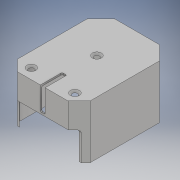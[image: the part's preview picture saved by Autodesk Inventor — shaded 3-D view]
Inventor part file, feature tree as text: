
AUTODESK INVENTOR PART (.ipt)
format: ipt  version: 2017 (Build 210142000, 142)  size: 454,144 bytes
history: native  units: mm
features: extrude x9, sketch x7, other x5, fillet x4, hole x3
ambient origin geometry x8: Origin, YZ Plane, XZ Plane, XY Plane, X Axis, Y Axis, Z Axis, Center Point
bodies: Body1 (feature_tree)
feature tree (28):
  other  "Твердое тело1"
  sketch  "Эскиз1"
  extrude  "Выдавливание1"  Depth=58.6mm
  extrude  "Выдавливание2"  Depth=77.0mm
  fillet  "Сопряжение1"  Radius=11.0mm
  extrude  "Выдавливание3"  Depth=11.0mm
  extrude  "Выдавливание4"  Depth=8.5mm
  extrude  "Выдавливание5"  Depth=8.5mm
  other  "Комбинировать1"
  hole  "Отверстие4"  [1 undecoded]
  hole  "Отверстие5"  [1 undecoded]
  hole  "Отверстие6"  [1 undecoded]
  fillet  "Сопряжение2"  Radius=11.0mm
  fillet  "Сопряжение3"  Radius=1.2mm
  extrude  "Выдавливание6"  Depth=1.5mm TaperAngle=0.0deg
  extrude  "Выдавливание7"  Depth=43.5mm TaperAngle=0.0deg
  extrude  "Выдавливание8"  Depth=1.0mm
  other  "Комбинировать2"
  fillet  "Сопряжение4"  Radius=4.0mm
  extrude  "Выдавливание9"  Depth=17.0mm
  other  "Твердое тело2"
  sketch  "Эскиз2"
  sketch  "Эскиз3"
  sketch  "Эскиз4"
  other  "Твердое тело3"
  sketch  "Эскиз5"
  sketch  "Эскиз6"
  sketch  "Эскиз7"
note: 3 required parameter values undecoded (feature->parameter linkage not recoverable at this tier; creation-order binding heuristic only, values carry confidence <= 0.55)
